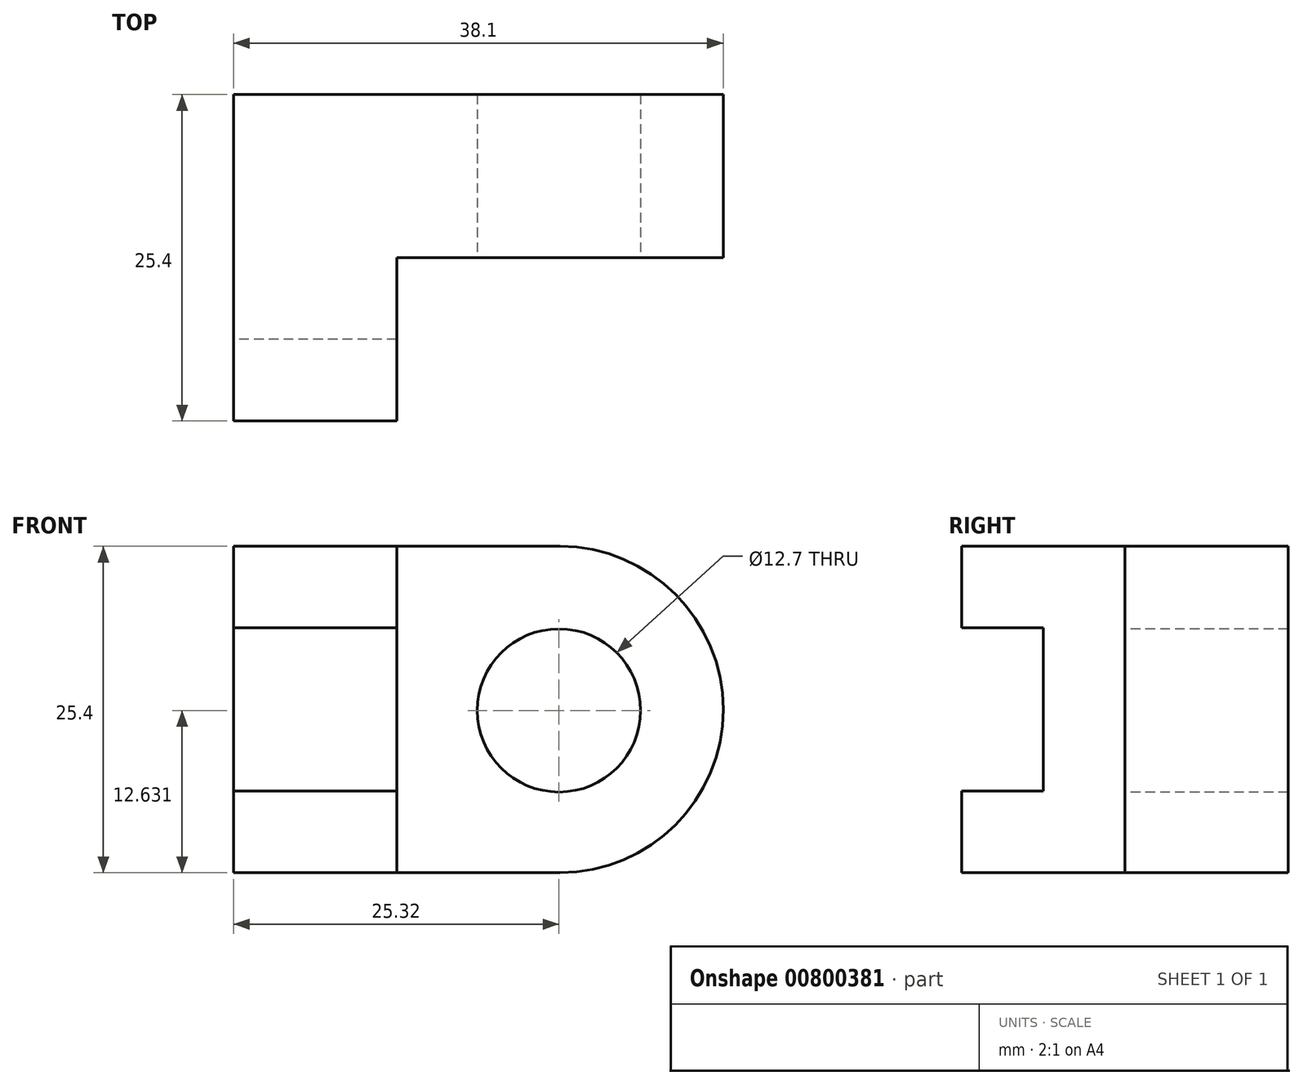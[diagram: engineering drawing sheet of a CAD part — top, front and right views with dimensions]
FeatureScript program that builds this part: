
annotation { "Feature Type Name" : "Feature", "Feature Type Description" : "" }
export const myFeature = defineFeature(function(context is Context, id is Id, definition is map)
    precondition{}
    {
        {
            var Q0;
            Q0=qCreatedBy(makeId("Right.planeOp"),FACE);
            var sketch = newSketch(context, id + "F0", { "sketchPlane" : qUnion([Q0])});
            skLineSegment(sketch, "E0", {"start": v(0, 0) * mm, "end": v(12.7, 0) * mm});
            skLineSegment(sketch, "E1", {"start": v(12.7, 0) * mm, "end": v(12.7, 25.4) * mm});
            skLineSegment(sketch, "E2", {"start": v(12.7, 25.4) * mm, "end": v(0, 25.4) * mm});
            skLineSegment(sketch, "E3", {"start": v(0, 25.4) * mm, "end": v(0, 19.05) * mm});
            skLineSegment(sketch, "E4", {"start": v(0, 19.05) * mm, "end": v(6.35, 19.05) * mm});
            skLineSegment(sketch, "E5", {"start": v(6.35, 19.05) * mm, "end": v(6.35, 6.35) * mm});
            skLineSegment(sketch, "E6", {"start": v(6.35, 6.35) * mm, "end": v(0, 6.35) * mm});
            skLineSegment(sketch, "E7", {"start": v(0, 6.35) * mm, "end": v(0, 0) * mm});
            skSolve(sketch);
        }
        {
            var Q0;
            Q0=makeQuery(id+"F0.imprint","IMPRINT",FACE,{"disambiguationData":[TD([[makeQuery(id+"F0.imprint","IMPRINT",EDGE,{"derivedFrom":sQuery(id+"F0.wireOp",EDGE,"E0")}),1.0]])]});
            extrude(context, id + "F1", {"entities" : qUnion([Q0]), "depth" : 12.7 * mm, "offsetDistance" : 25.4 * mm});
        }
        {
            var Q0;
            Q0=qCreatedBy(makeId("Top.planeOp"),FACE);
            var sketch = newSketch(context, id + "F2", { "sketchPlane" : qUnion([Q0])});
            skLineSegment(sketch, "E8", {"start": v(0, 0) * mm, "end": v(0, 25.4) * mm});
            skLineSegment(sketch, "E9", {"start": v(0, 25.4) * mm, "end": v(38.1, 25.4) * mm});
            skLineSegment(sketch, "E10", {"start": v(38.1, 25.4) * mm, "end": v(38.1, 12.7) * mm});
            skLineSegment(sketch, "E11", {"start": v(38.1, 12.7) * mm, "end": v(0, 12.7) * mm});
            skSolve(sketch);
        }
        {
            var Q0;
            {var subQ0=sQuery(id+"F2.wireOp",EDGE,"E9");Q0=makeQuery(id+"F2.imprint","IMPRINT",FACE,{"disambiguationData":[TD([[makeQuery(id+"F2.imprint","IMPRINT",EDGE,{"derivedFrom":subQ0}),-1.0]])]});}
            extrude(context, id + "F3", {"entities" : qUnion([Q0]), "operationType" : NewBodyOperationType.ADD, "depth" : 25.4 * mm, "offsetDistance" : 25.4 * mm});
        }
        {
            var Q0;
            Q0=makeQuery(id+"F3.opExtrude","SWEPT_FACE",FACE,{"disambiguationData":[OSD([sQuery(id+"F2.wireOp",EDGE,"E11")])]});
            var sketch = newSketch(context, id + "F4", { "sketchPlane" : qUnion([Q0])});
            skLineSegment(sketch, "E12", {"start": v(12.7, 25.4) * mm, "end": v(25.4, 25.4) * mm, "construction": true});
            skLineSegment(sketch, "E13", {"start": v(12.7, 0) * mm, "end": v(25.4, 0) * mm, "construction": true});
            skLineSegment(sketch, "E14", {"start": v(25.4, 25.4) * mm, "end": v(25.4, 0) * mm, "construction": true});
            skLineSegment(sketch, "E15", {"start": v(38.1, 12.7) * mm, "end": v(12.7, 12.7) * mm, "construction": true});
            skArc(sketch, "E16", {"start": v(38.1, 12.7) * mm, "mid": v(34.38, 21.68) * mm, "end": v(25.4, 25.4) * mm});
            skArc(sketch, "E17", {"start": v(25.4, 0) * mm, "mid": v(34.38, 3.72) * mm, "end": v(38.1, 12.7) * mm});
            skSolve(sketch);
        }
        {
            var Q0;
            {var subQ0=sQuery(id+"F4.wireOp",EDGE,"E16");Q0=makeQuery(id+"F4.imprint","IMPRINT",FACE,{"disambiguationData":[TD([[makeQuery(id+"F4.imprint","IMPRINT",EDGE,{"derivedFrom":subQ0}),-1.0]])]});}
            extrude(context, id + "F5", {"entities" : qUnion([Q0]), "operationType" : NewBodyOperationType.REMOVE, "oppositeDirection" : true, "depth" : 25.4 * mm, "offsetDistance" : 25.4 * mm});
        }
        {
            var Q0;
            {var subQ0=sQuery(id+"F4.wireOp",EDGE,"E17");Q0=makeQuery(id+"F4.imprint","IMPRINT",FACE,{"disambiguationData":[TD([[makeQuery(id+"F4.imprint","IMPRINT",EDGE,{"derivedFrom":subQ0}),-1.0]])]});}
            extrude(context, id + "F6", {"entities" : qUnion([Q0]), "operationType" : NewBodyOperationType.REMOVE, "oppositeDirection" : true, "depth" : 25.4 * mm, "offsetDistance" : 25.4 * mm});
        }
        {
            var Q0;
            {var subQ4=sQuery(id+"F4.wireOp",EDGE,"E16");Q0=makeQuery(id+"F4.imprint","IMPRINT",FACE,{"disambiguationData":[TD([[makeQuery(id+"F4.imprint","IMPRINT",EDGE,{"derivedFrom":subQ4}),1.0]])]});}
            var sketch = newSketch(context, id + "F7", { "sketchPlane" : qUnion([Q0])});
            skCircle(sketch, "E18", {"center": v(25.32, 12.63) * mm, "radius": 6.35 * mm});
            skSolve(sketch);
        }
        {
            var Q0;
            Q0=makeQuery(id+"F7.imprint","IMPRINT",FACE,{"disambiguationData":[TD([[makeQuery(id+"F7.imprint","IMPRINT",EDGE,{"derivedFrom":sQuery(id+"F7.wireOp",EDGE,"E18")}),1.0]])]});
            var Q1;
            Q1=sQuery(id+"F7.wireOp",EDGE,"E18");
            extrude(context, id + "F8", {"entities" : qUnion([Q0]), "operationType" : NewBodyOperationType.REMOVE, "surfaceEntities" : qUnion([Q1]), "oppositeDirection" : true, "depth" : 25.4 * mm, "offsetDistance" : 25.4 * mm});
        }
    });
